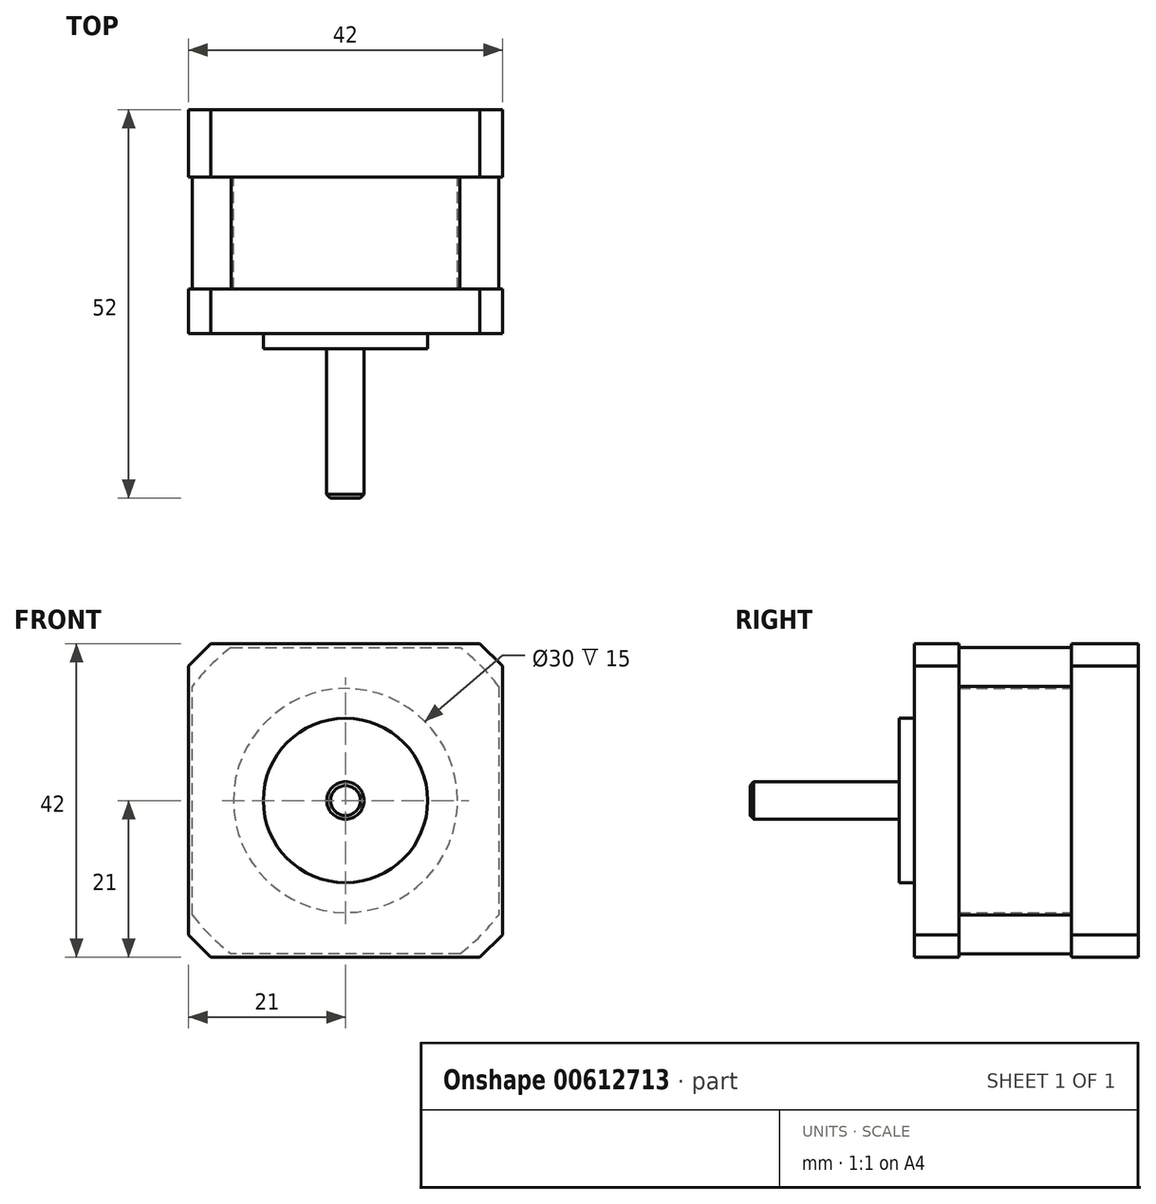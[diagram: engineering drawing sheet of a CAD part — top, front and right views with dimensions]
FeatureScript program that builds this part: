
annotation { "Feature Type Name" : "Feature", "Feature Type Description" : "" }
export const myFeature = defineFeature(function(context is Context, id is Id, definition is map)
    precondition{}
    {
        {
            var Q0;
            Q0=qCreatedBy(makeId("Front.planeOp"),FACE);
            var sketch = newSketch(context, id + "F0", { "sketchPlane" : qUnion([Q0])});
            skLineSegment(sketch, "E0.bottom", {"start": v(21, 21) * mm, "end": v(-21, 21) * mm});
            skLineSegment(sketch, "E0.top", {"start": v(21, -21) * mm, "end": v(-21, -21) * mm});
            skLineSegment(sketch, "E0.left", {"start": v(21, 21) * mm, "end": v(21, -21) * mm});
            skLineSegment(sketch, "E0.right", {"start": v(-21, 21) * mm, "end": v(-21, -21) * mm});
            skPoint(sketch, "E0.middle", {"position": v(0, 0) * mm});
            skSolve(sketch);
        }
        {
            var Q0;
            Q0=makeQuery(id+"F0.imprint","IMPRINT",FACE,{"disambiguationData":[TD([[makeQuery(id+"F0.imprint","IMPRINT",EDGE,{"derivedFrom":sQuery(id+"F0.wireOp",EDGE,"E0.bottom")}),1.0]])]});
            extrude(context, id + "F1", {"entities" : qUnion([Q0]), "depth" : 9 * mm, "offsetDistance" : 25 * mm});
        }
        {
            var Q0;
            Q0=makeQuery(id+"F1.opExtrude","SWEPT_EDGE",EDGE,{"disambiguationData":[OSD([sQuery(id+"F0.wireOp",EDGE,"E0.bottom"),sQuery(id+"F0.wireOp",EDGE,"E0.right")])]});
            var Q1;
            Q1=makeQuery(id+"F1.opExtrude","SWEPT_EDGE",EDGE,{"disambiguationData":[OSD([sQuery(id+"F0.wireOp",EDGE,"E0.bottom"),sQuery(id+"F0.wireOp",EDGE,"E0.left")])]});
            var Q2;
            Q2=makeQuery(id+"F1.opExtrude","SWEPT_EDGE",EDGE,{"disambiguationData":[OSD([sQuery(id+"F0.wireOp",EDGE,"E0.top"),sQuery(id+"F0.wireOp",EDGE,"E0.left")])]});
            var Q3;
            Q3=makeQuery(id+"F1.opExtrude","SWEPT_EDGE",EDGE,{"disambiguationData":[OSD([sQuery(id+"F0.wireOp",EDGE,"E0.top"),sQuery(id+"F0.wireOp",EDGE,"E0.right")])]});
            chamfer(context, id + "F2", {"entities" : qUnion([Q0, Q1, Q2, Q3]), "width" : 3 * mm, "tangentPropagation" : true});
        }
        {
            var Q0;
            Q0=makeQuery(id+"F1.opExtrude","CAP_FACE",FACE,{"disambiguationData":[OSD([sQuery(id+"F0.wireOp",EDGE,"E0.bottom"),sQuery(id+"F0.wireOp",EDGE,"E0.top"),sQuery(id+"F0.wireOp",EDGE,"E0.left"),sQuery(id+"F0.wireOp",EDGE,"E0.right")])],"isStart":false});
            var sketch = newSketch(context, id + "F3", { "sketchPlane" : qUnion([Q0])});
            skLineSegment(sketch, "E1", {"start": v(-15.3, 20.5) * mm, "end": v(15.3, 20.5) * mm});
            skLineSegment(sketch, "E2", {"start": v(20.5, 15.3) * mm, "end": v(20.5, -15.3) * mm});
            skLineSegment(sketch, "E3", {"start": v(15.3, -20.5) * mm, "end": v(-15.3, -20.5) * mm});
            skLineSegment(sketch, "E4", {"start": v(-20.5, -15.3) * mm, "end": v(-20.5, 15.3) * mm});
            skLineSegment(sketch, "E5", {"start": v(-21, 0) * mm, "end": v(-20.5, 0) * mm, "construction": true});
            skLineSegment(sketch, "E6", {"start": v(0, 21) * mm, "end": v(0, 20.5) * mm, "construction": true});
            skPoint(sketch, "E6.startSnap0", {"position": v(0, 20.5) * mm});
            skPoint(sketch, "E6.endSnap0", {"position": v(0, 21) * mm});
            skLineSegment(sketch, "E7", {"start": v(20.5, 0) * mm, "end": v(21, 0) * mm, "construction": true});
            skLineSegment(sketch, "E8", {"start": v(0, -21) * mm, "end": v(0, -20.5) * mm, "construction": true});
            skCircle(sketch, "E9", {"center": v(0, 0) * mm, "radius": 25.58 * mm});
            skCircle(sketch, "E10", {"center": v(0, 0) * mm, "radius": 15 * mm});
            skSolve(sketch);
        }
        {
            var Q0;
            {var subQ4=sQuery(id+"F3.wireOp",EDGE,"E1");Q0=makeQuery(id+"F3.imprint","IMPRINT",FACE,{"disambiguationData":[TD([[makeQuery(id+"F3.imprint","IMPRINT",EDGE,{"derivedFrom":subQ4}),-1.0]])]});}
            extrude(context, id + "F4", {"entities" : qUnion([Q0]), "depth" : 15 * mm, "offsetDistance" : 25 * mm});
        }
        {
            var Q0;
            Q0=makeQuery(id+"F4.opExtrude","CAP_FACE",FACE,{"disambiguationData":[OSD([sQuery(id+"F3.wireOp",EDGE,"E1"),sQuery(id+"F3.wireOp",EDGE,"E2"),sQuery(id+"F3.wireOp",EDGE,"E3"),sQuery(id+"F3.wireOp",EDGE,"E4"),sQuery(id+"F3.wireOp",EDGE,"E9")])],"isStart":false});
            var sketch = newSketch(context, id + "F5", { "sketchPlane" : qUnion([Q0])});
            skLineSegment(sketch, "E11.0.0", {"start": v(-21, 18) * mm, "end": v(-21, -18) * mm});
            skLineSegment(sketch, "E11.0.1", {"start": v(-21, -18) * mm, "end": v(-18, -21) * mm});
            skLineSegment(sketch, "E11.0.2", {"start": v(-18, -21) * mm, "end": v(18, -21) * mm});
            skLineSegment(sketch, "E11.0.3", {"start": v(18, -21) * mm, "end": v(21, -18) * mm});
            skLineSegment(sketch, "E11.0.4", {"start": v(21, -18) * mm, "end": v(21, 18) * mm});
            skLineSegment(sketch, "E11.0.5", {"start": v(21, 18) * mm, "end": v(18, 21) * mm});
            skLineSegment(sketch, "E11.0.6", {"start": v(18, 21) * mm, "end": v(-18, 21) * mm});
            skLineSegment(sketch, "E11.0.7", {"start": v(-18, 21) * mm, "end": v(-21, 18) * mm});
            skSolve(sketch);
        }
        {
            var Q0;
            Q0 = qSketchRegion(id + "F5", true);
            extrude(context, id + "F6", {"entities" : qUnion([Q0]), "flatOperationType" : FlatOperationType.REMOVE, "depth" : 6 * mm, "offsetDistance" : 25 * mm, "domain" : OperationDomain.MODEL});
        }
        {
            var Q0;
            Q0=makeQuery(id+"F6.opExtrude","CAP_FACE",FACE,{"disambiguationData":[OSD([sQuery(id+"F5.wireOp",EDGE,"E11.0.0"),sQuery(id+"F5.wireOp",EDGE,"E11.0.1"),sQuery(id+"F5.wireOp",EDGE,"E11.0.2"),sQuery(id+"F5.wireOp",EDGE,"E11.0.3"),sQuery(id+"F5.wireOp",EDGE,"E11.0.4"),sQuery(id+"F5.wireOp",EDGE,"E11.0.5"),sQuery(id+"F5.wireOp",EDGE,"E11.0.6"),sQuery(id+"F5.wireOp",EDGE,"E11.0.7")])],"isStart":false});
            var sketch = newSketch(context, id + "F7", { "sketchPlane" : qUnion([Q0])});
            skCircle(sketch, "E12", {"center": v(0, 0) * mm, "radius": 11 * mm});
            skSolve(sketch);
        }
        {
            var Q0;
            Q0=makeQuery(id+"F7.imprint","IMPRINT",FACE,{"disambiguationData":[TD([[makeQuery(id+"F7.imprint","IMPRINT",EDGE,{"derivedFrom":sQuery(id+"F7.wireOp",EDGE,"E12")}),1.0]])]});
            extrude(context, id + "F8", {"entities" : qUnion([Q0]), "operationType" : NewBodyOperationType.ADD, "depth" : 2 * mm, "offsetDistance" : 25 * mm});
        }
        {
            var Q0;
            Q0=makeQuery(id+"F8.opExtrude","CAP_FACE",FACE,{"disambiguationData":[OSD([sQuery(id+"F7.wireOp",EDGE,"E12")])],"isStart":false});
            var sketch = newSketch(context, id + "F9", { "sketchPlane" : qUnion([Q0])});
            skCircle(sketch, "E13", {"center": v(0, 0) * mm, "radius": 2.5 * mm});
            skSolve(sketch);
        }
        {
            var Q0;
            Q0=makeQuery(id+"F9.imprint","IMPRINT",FACE,{"disambiguationData":[TD([[makeQuery(id+"F9.imprint","IMPRINT",EDGE,{"derivedFrom":sQuery(id+"F9.wireOp",EDGE,"E13")}),1.0]])]});
            extrude(context, id + "F10", {"entities" : qUnion([Q0]), "depth" : 20 * mm, "offsetDistance" : 25 * mm});
        }
        {
            var Q0;
            Q0=makeQuery(id+"F10.opExtrude","CAP_EDGE",EDGE,{"disambiguationData":[OSD([sQuery(id+"F9.wireOp",EDGE,"E13")])],"isStart":false});
            chamfer(context, id + "F11", {"entities" : qUnion([Q0]), "width" : 0.5 * mm, "tangentPropagation" : true});
        }
    });
